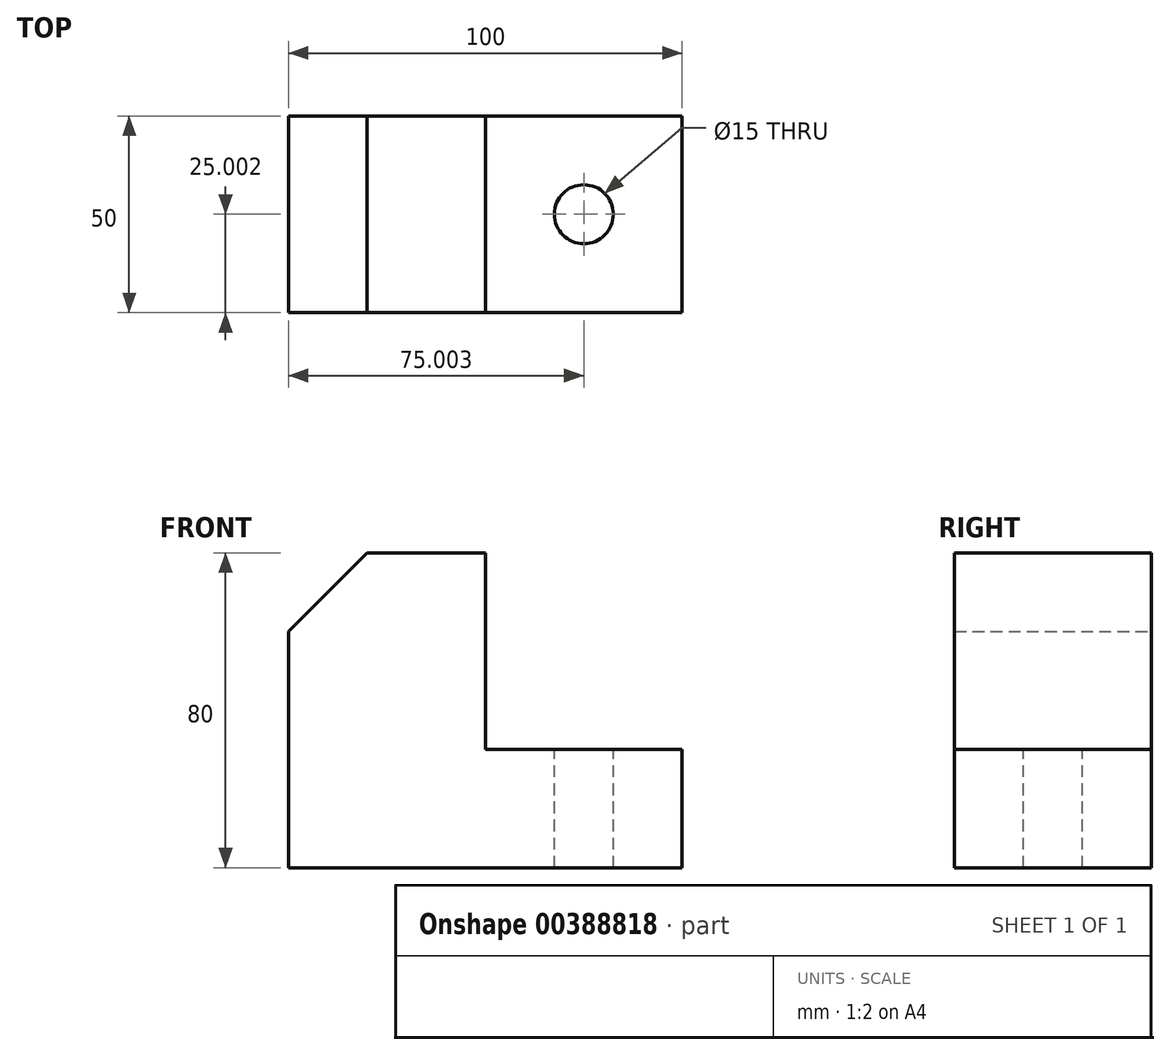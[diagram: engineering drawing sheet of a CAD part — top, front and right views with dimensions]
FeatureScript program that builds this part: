
annotation { "Feature Type Name" : "Feature", "Feature Type Description" : "" }
export const myFeature = defineFeature(function(context is Context, id is Id, definition is map)
    precondition{}
    {
        {
            var Q0;
            Q0=qCreatedBy(makeId("Top.planeOp"),FACE);
            var sketch = newSketch(context, id + "F0", { "sketchPlane" : qUnion([Q0])});
            skLineSegment(sketch, "E0.bottom", {"start": v(-44.24, -0.06) * mm, "end": v(55.76, -0.06) * mm});
            skLineSegment(sketch, "E0.top", {"start": v(-44.24, -50.06) * mm, "end": v(55.76, -50.06) * mm});
            skLineSegment(sketch, "E0.left", {"start": v(-44.24, -0.06) * mm, "end": v(-44.24, -50.06) * mm});
            skLineSegment(sketch, "E0.right", {"start": v(55.76, -0.06) * mm, "end": v(55.76, -50.06) * mm});
            skSolve(sketch);
        }
        {
            var Q0;
            Q0 = qSketchRegion(id + "F0", true);
            extrude(context, id + "F1", {"entities" : qUnion([Q0]), "depth" : 80 * mm});
        }
        {
            var Q0;
            Q0=makeQuery(id+"F1.opExtrude","SWEPT_FACE",FACE,{"disambiguationData":[OSD([sQuery(id+"F0.wireOp",EDGE,"E0.top")])]});
            var sketch = newSketch(context, id + "F2", { "sketchPlane" : qUnion([Q0])});
            skLineSegment(sketch, "E1.bottom", {"start": v(55.76, 80) * mm, "end": v(5.76, 80) * mm});
            skLineSegment(sketch, "E1.top", {"start": v(55.76, 30) * mm, "end": v(5.76, 30) * mm});
            skLineSegment(sketch, "E1.left", {"start": v(55.76, 80) * mm, "end": v(55.76, 30) * mm});
            skLineSegment(sketch, "E1.right", {"start": v(5.76, 80) * mm, "end": v(5.76, 30) * mm});
            skSolve(sketch);
        }
        {
            var Q0;
            Q0 = qSketchRegion(id + "F2", true);
            var Q1;
            Q1=makeQuery(id+"F1.opExtrude","SWEPT_FACE",FACE,{"disambiguationData":[OSD([sQuery(id+"F0.wireOp",EDGE,"E0.bottom")])]});
            extrude(context, id + "F3", {"entities" : qUnion([Q0]), "operationType" : NewBodyOperationType.REMOVE, "endBound" : BoundingType.UP_TO_SURFACE, "oppositeDirection" : true, "endBoundEntityFace" : qUnion([Q1]), "depth" : 25 * mm});
        }
        {
            var Q0;
            Q0=makeQuery(id+"F1.opExtrude","CAP_EDGE",EDGE,{"disambiguationData":[OSD([sQuery(id+"F0.wireOp",EDGE,"E0.left")])],"isStart":false});
            chamfer(context, id + "F4", {"entities" : qUnion([Q0]), "width" : 20 * mm, "tangentPropagation" : true});
        }
        {
            var Q0;
            Q0=makeQuery(id+"F3.boolean.opBoolean","COPY",FACE,{"derivedFrom":makeQuery(id+"F3.opExtrude","SWEPT_FACE",FACE,{"disambiguationData":[OSD([sQuery(id+"F2.wireOp",EDGE,"E1.top")])]})});
            var sketch = newSketch(context, id + "F5", { "sketchPlane" : qUnion([Q0])});
            skCircle(sketch, "E2", {"center": v(30.76, -25.06) * mm, "radius": 7.5 * mm});
            skSolve(sketch);
        }
        {
            var Q0;
            Q0 = qSketchRegion(id + "F5", true);
            var Q1;
            Q1=makeQuery(id+"F1.opExtrude","CAP_FACE",FACE,{"disambiguationData":[OSD([sQuery(id+"F0.wireOp",EDGE,"E0.bottom"),sQuery(id+"F0.wireOp",EDGE,"E0.top"),sQuery(id+"F0.wireOp",EDGE,"E0.left"),sQuery(id+"F0.wireOp",EDGE,"E0.right")])],"isStart":true});
            extrude(context, id + "F6", {"entities" : qUnion([Q0]), "operationType" : NewBodyOperationType.REMOVE, "endBound" : BoundingType.UP_TO_SURFACE, "oppositeDirection" : true, "endBoundEntityFace" : qUnion([Q1]), "depth" : 25 * mm});
        }
    });
